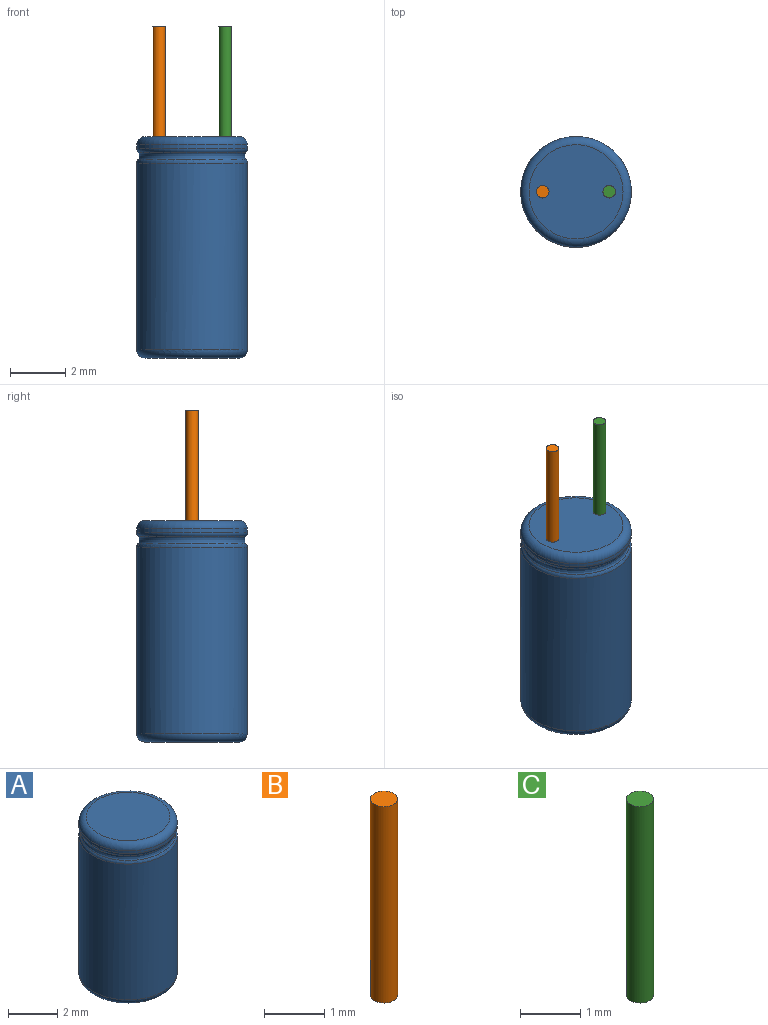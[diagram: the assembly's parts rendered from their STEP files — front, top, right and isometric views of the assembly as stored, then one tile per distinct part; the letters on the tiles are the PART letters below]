
ASSEMBLY  parts=3 mates=2
PART A: 9 faces, bbox 4.3x4.3x8 mm
  f0: cylinder r=2mm len=6.75mm, axis (0,0,-1), area 84.8mm2, adj f2,f7
  f1: plane 3.4x3.4mm, normal (0,0,-1), area 9.1mm2, adj f2
  f2: torus R=1.7mm, axis (0,0,1), area 5.6mm2, adj f0,f1
  f3: bspline ~3.88x3.82mm, area 3.2mm2, adj f7,f8
  f4: plane 3.4x3.4mm, normal (0,0,1), area 9.1mm2, adj f5
  f5: torus R=1.7mm, axis (0,0,1), area 5.6mm2, adj f4,f6
  f6: cylinder r=2mm len=4mm, axis (0,0,-1), area 1.6mm2, adj f5,f8
  f7: torus R=1.8mm, axis (0,0,-1), area 1.9mm2, adj f0,f3
  f8: torus R=1.8mm, axis (0,0,1), area 1.9mm2, adj f3,f6
PART B: 3 faces, bbox 0.5x0.5x4 mm
  f0: cylinder r=0.23mm len=4mm, axis (0,0,-1), area 5.7mm2, adj f1,f2
  f1: plane 0.45x0.45mm, normal (0,0,1), area 0.2mm2, adj f0
  f2: plane 0.45x0.45mm, normal (0,0,-1), area 0.2mm2, adj f0
PART C: 3 faces, bbox 0.5x0.5x4 mm
  f0: cylinder r=0.23mm len=4mm, axis (0,0,-1), area 5.7mm2, adj f1,f2
  f1: plane 0.45x0.45mm, normal (0,0,1), area 0.2mm2, adj f0
  f2: plane 0.45x0.45mm, normal (0,0,-1), area 0.2mm2, adj f0
PLACE A t=(-1.84,-1.54,0.81)mm
PLACE B t=(-4.04,-1.54,-1.19)mm
PLACE C t=(0.36,-1.54,-1.19)mm
MATE fastened B.f0 <-> A.f4  axis (0,0,-1) through (-3.04,-1.54,8.81)mm
MATE fastened C.f0 <-> A.f4  axis (0,0,-1) through (-0.64,-1.54,8.81)mm
